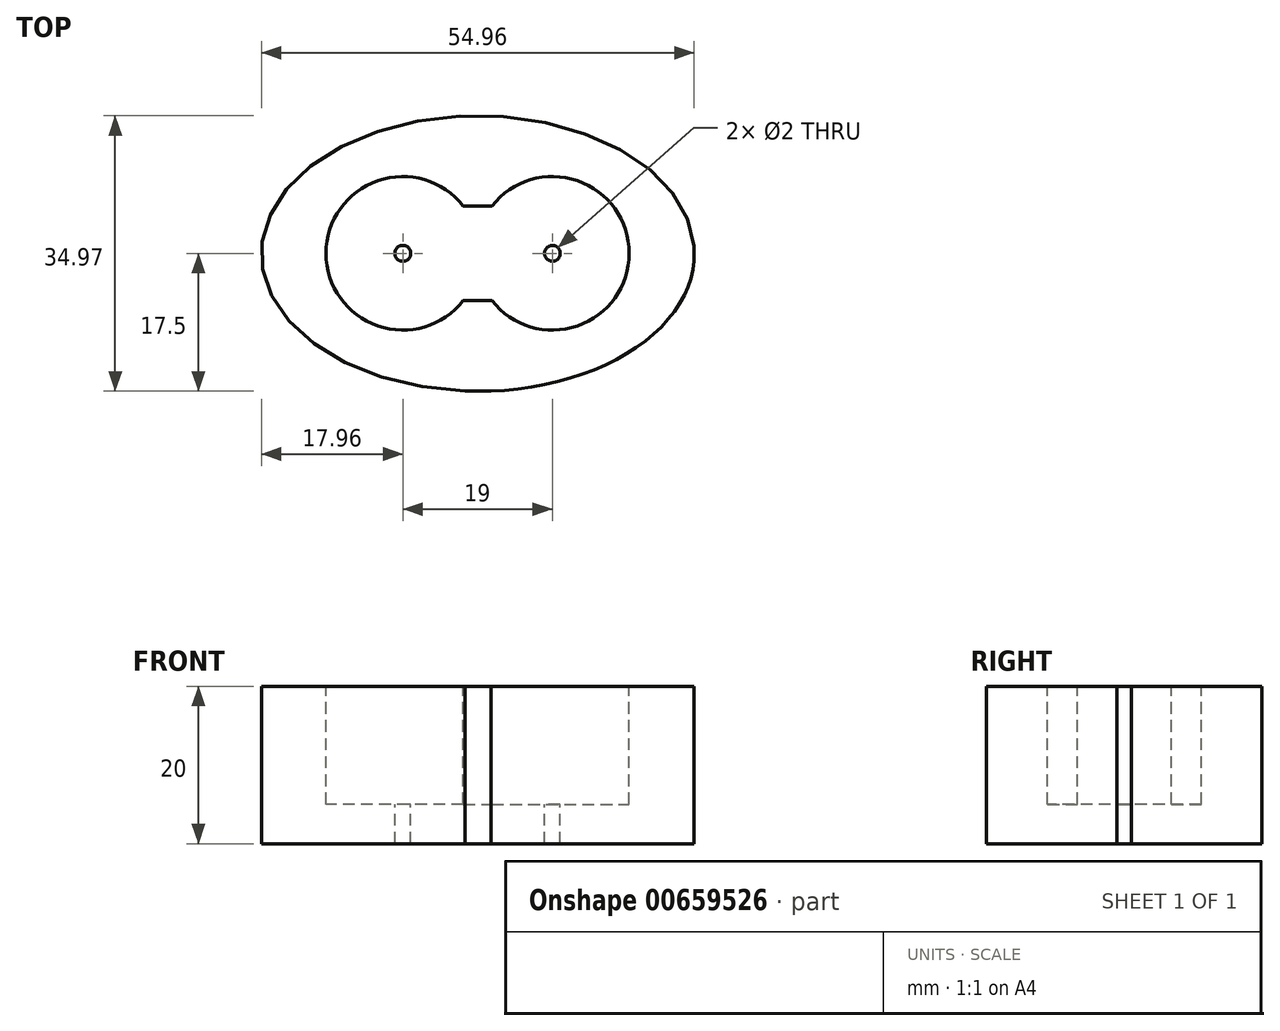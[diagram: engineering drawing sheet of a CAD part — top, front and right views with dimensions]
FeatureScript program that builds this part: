
annotation { "Feature Type Name" : "Feature", "Feature Type Description" : "" }
export const myFeature = defineFeature(function(context is Context, id is Id, definition is map)
    precondition{}
    {
        {
            var Q0;
            Q0=qCreatedBy(makeId("Top.planeOp"),FACE);
            var sketch = newSketch(context, id + "F0", { "sketchPlane" : qUnion([Q0])});
            skLineSegment(sketch, "E0.bottom", {"start": v(0, 35) * mm, "end": v(55, 35) * mm});
            skLineSegment(sketch, "E0.top", {"start": v(0, 0) * mm, "end": v(55, 0) * mm});
            skLineSegment(sketch, "E0.left", {"start": v(0, 35) * mm, "end": v(0, 0) * mm});
            skLineSegment(sketch, "E0.right", {"start": v(55, 35) * mm, "end": v(55, 0) * mm});
            skSolve(sketch);
        }
        {
            var Q0;
            Q0=qSketchRegion(id+"F0",true);
            var Q1;
            Q1=makeQuery(id+"F0.imprint","IMPRINT",FACE,{"disambiguationData":[TD([[makeQuery(id+"F0.imprint","IMPRINT",EDGE,{"derivedFrom":sQuery(id+"F0.wireOp",EDGE,"E0.bottom")}),-1.0]])]});
            extrude(context, id + "F1", {"entities" : qUnion([Q0, Q1]), "depth" : 20 * mm, "offsetDistance" : 25 * mm});
        }
        {
            var Q0;
            Q0=makeQuery(id+"F1.opExtrude","CAP_FACE",FACE,{"disambiguationData":[OSD([sQuery(id+"F0.wireOp",EDGE,"E0.bottom"),sQuery(id+"F0.wireOp",EDGE,"E0.top"),sQuery(id+"F0.wireOp",EDGE,"E0.left"),sQuery(id+"F0.wireOp",EDGE,"E0.right")])],"isStart":false});
            var sketch = newSketch(context, id + "F2", { "sketchPlane" : qUnion([Q0])});
            skCircle(sketch, "E1", {"center": v(18, 17.5) * mm, "radius": 9.75 * mm});
            skCircle(sketch, "E2", {"center": v(37, 17.5) * mm, "radius": 9.75 * mm});
            skLineSegment(sketch, "E3.bottom", {"start": v(18.12, 23.5) * mm, "end": v(37.12, 23.5) * mm});
            skLineSegment(sketch, "E3.top", {"start": v(18.12, 11.5) * mm, "end": v(37.12, 11.5) * mm});
            skLineSegment(sketch, "E3.left", {"start": v(18.12, 23.5) * mm, "end": v(18.12, 11.5) * mm});
            skLineSegment(sketch, "E3.right", {"start": v(37.12, 23.5) * mm, "end": v(37.12, 11.5) * mm});
            skCircle(sketch, "E4", {"center": v(18, 17.5) * mm, "radius": 1 * mm});
            skCircle(sketch, "E5", {"center": v(37, 17.5) * mm, "radius": 1 * mm});
            skSolve(sketch);
        }
        {
            var Q0;
            {var subQ0=sQuery(id+"F2.wireOp",EDGE,"E2");var subQ1=sQuery(id+"F2.wireOp",EDGE,"E1");var subQ2=makeQuery(id+"F2.imprint","INTERSECT",VERTEX,{"disambiguationData":[OD(0.0)],"derivedFrom":[subQ1,subQ0]});Q0=makeQuery(id+"F2.imprint","IMPRINT",FACE,{"disambiguationData":[TD([[makeQuery(id+"F2.imprint","IMPRINT",EDGE,{"disambiguationData":[TD([[subQ2,-1.0]])],"derivedFrom":subQ1}),-1.0]])]});}
            var Q1;
            {var subQ0=sQuery(id+"F2.wireOp",EDGE,"E2");var subQ1=sQuery(id+"F2.wireOp",EDGE,"E1");var subQ2=makeQuery(id+"F2.imprint","INTERSECT",VERTEX,{"disambiguationData":[OD(0.0)],"derivedFrom":[subQ1,subQ0]});Q1=makeQuery(id+"F2.imprint","IMPRINT",FACE,{"disambiguationData":[TD([[makeQuery(id+"F2.imprint","IMPRINT",EDGE,{"disambiguationData":[TD([[subQ2,1.0]])],"derivedFrom":subQ1}),1.0]])]});}
            var Q2;
            {var subQ0=sQuery(id+"F2.wireOp",EDGE,"E2");var subQ1=sQuery(id+"F2.wireOp",EDGE,"E1");var subQ2=makeQuery(id+"F2.imprint","INTERSECT",VERTEX,{"disambiguationData":[OD(0.0)],"derivedFrom":[subQ1,subQ0]});Q2=makeQuery(id+"F2.imprint","IMPRINT",FACE,{"disambiguationData":[TD([[makeQuery(id+"F2.imprint","IMPRINT",EDGE,{"disambiguationData":[TD([[subQ2,-1.0]])],"derivedFrom":subQ1}),1.0]])]});}
            var Q3;
            {var subQ5=sQuery(id+"F2.wireOp",EDGE,"E3.left");Q3=makeQuery(id+"F2.imprint","IMPRINT",FACE,{"disambiguationData":[TD([[makeQuery(id+"F2.imprint","IMPRINT",EDGE,{"derivedFrom":subQ5}),-1.0]])]});}
            var Q4;
            {var subQ0=sQuery(id+"F2.wireOp",EDGE,"E3.right");Q4=makeQuery(id+"F2.imprint","IMPRINT",FACE,{"disambiguationData":[TD([[makeQuery(id+"F2.imprint","IMPRINT",EDGE,{"derivedFrom":subQ0}),-1.0]])]});}
            var Q5;
            {var subQ0=sQuery(id+"F2.wireOp",EDGE,"E3.top");var subQ1=sQuery(id+"F2.wireOp",EDGE,"E1");var subQ2=makeQuery(id+"F2.imprint","INTERSECT",VERTEX,{"derivedFrom":[subQ1,subQ0]});Q5=makeQuery(id+"F2.imprint","IMPRINT",FACE,{"disambiguationData":[TD([[makeQuery(id+"F2.imprint","IMPRINT",EDGE,{"disambiguationData":[TD([[subQ2,-1.0]])],"derivedFrom":subQ1}),-1.0]])]});}
            var Q6;
            {var subQ5=sQuery(id+"F2.wireOp",EDGE,"E3.right");Q6=makeQuery(id+"F2.imprint","IMPRINT",FACE,{"disambiguationData":[TD([[makeQuery(id+"F2.imprint","IMPRINT",EDGE,{"derivedFrom":subQ5}),1.0]])]});}
            extrude(context, id + "F3", {"entities" : qUnion([Q0, Q1, Q2, Q3, Q4, Q5, Q6]), "operationType" : NewBodyOperationType.REMOVE, "oppositeDirection" : true, "depth" : 15 * mm, "offsetDistance" : 25 * mm});
        }
        {
            var Q0;
            Q0=makeQuery(id+"F3.boolean.opBoolean","SPLIT",FACE,{"disambiguationData":[TD([makeQuery(id+"F3.opExtrude","SWEPT_FACE",FACE,{"disambiguationData":[OSD([sQuery(id+"F2.wireOp",EDGE,"E4")])]})])],"derivedFrom":makeQuery(id+"F1.opExtrude","CAP_FACE",FACE,{"disambiguationData":[OSD([sQuery(id+"F0.wireOp",EDGE,"E0.bottom"),sQuery(id+"F0.wireOp",EDGE,"E0.top"),sQuery(id+"F0.wireOp",EDGE,"E0.left"),sQuery(id+"F0.wireOp",EDGE,"E0.right")])],"isStart":false})});
            var Q1;
            Q1=makeQuery(id+"F3.boolean.opBoolean","SPLIT",FACE,{"disambiguationData":[TD([makeQuery(id+"F3.opExtrude","SWEPT_FACE",FACE,{"disambiguationData":[OSD([sQuery(id+"F2.wireOp",EDGE,"E5")])]})])],"derivedFrom":makeQuery(id+"F1.opExtrude","CAP_FACE",FACE,{"disambiguationData":[OSD([sQuery(id+"F0.wireOp",EDGE,"E0.bottom"),sQuery(id+"F0.wireOp",EDGE,"E0.top"),sQuery(id+"F0.wireOp",EDGE,"E0.left"),sQuery(id+"F0.wireOp",EDGE,"E0.right")])],"isStart":false})});
            extrude(context, id + "F4", {"entities" : qUnion([Q0, Q1]), "operationType" : NewBodyOperationType.REMOVE, "oppositeDirection" : true, "depth" : 20 * mm, "offsetDistance" : 25 * mm});
        }
        {
            var Q0;
            Q0=makeQuery(id+"F1.opExtrude","CAP_FACE",FACE,{"disambiguationData":[OSD([sQuery(id+"F0.wireOp",EDGE,"E0.bottom"),sQuery(id+"F0.wireOp",EDGE,"E0.top"),sQuery(id+"F0.wireOp",EDGE,"E0.left"),sQuery(id+"F0.wireOp",EDGE,"E0.right")])],"isStart":false});
            var sketch = newSketch(context, id + "F5", { "sketchPlane" : qUnion([Q0])});
            skEllipse(sketch, "E6", {"center": v(27.54, 17.47) * mm, "majorRadius": 27.5 * mm, "minorRadius": 17.5 * mm, "majorAxis": v(1, 0)});
            skSolve(sketch);
        }
        {
            var Q0;
            {var subQ0=makeQuery(id+"F1.opExtrude","CAP_EDGE",EDGE,{"disambiguationData":[OSD([sQuery(id+"F0.wireOp",EDGE,"E0.bottom")])],"isStart":false});Q0=makeQuery(id+"F5.imprint","IMPRINT",FACE,{"disambiguationData":[TD([[makeQuery(id+"F5.imprint","IMPRINT",EDGE,{"derivedFrom":subQ0}),-1.0]])]});}
            var Q1;
            {var subQ0=sQuery(id+"F5.wireOp",EDGE,"E6");var subQ1=makeQuery(id+"F1.opExtrude","CAP_EDGE",EDGE,{"disambiguationData":[OSD([sQuery(id+"F0.wireOp",EDGE,"E0.top")])],"isStart":false});var subQ2=makeQuery(id+"F5.imprint","INTERSECT",VERTEX,{"disambiguationData":[OD(1.0)],"derivedFrom":[subQ1,subQ0]});Q1=makeQuery(id+"F5.imprint","IMPRINT",FACE,{"disambiguationData":[TD([[makeQuery(id+"F5.imprint","IMPRINT",EDGE,{"disambiguationData":[TD([[subQ2,-1.0]])],"derivedFrom":subQ0}),-1.0]])]});}
            extrude(context, id + "F6", {"entities" : qUnion([Q0, Q1]), "operationType" : NewBodyOperationType.REMOVE, "oppositeDirection" : true, "depth" : 25 * mm, "offsetDistance" : 25 * mm});
        }
    });
